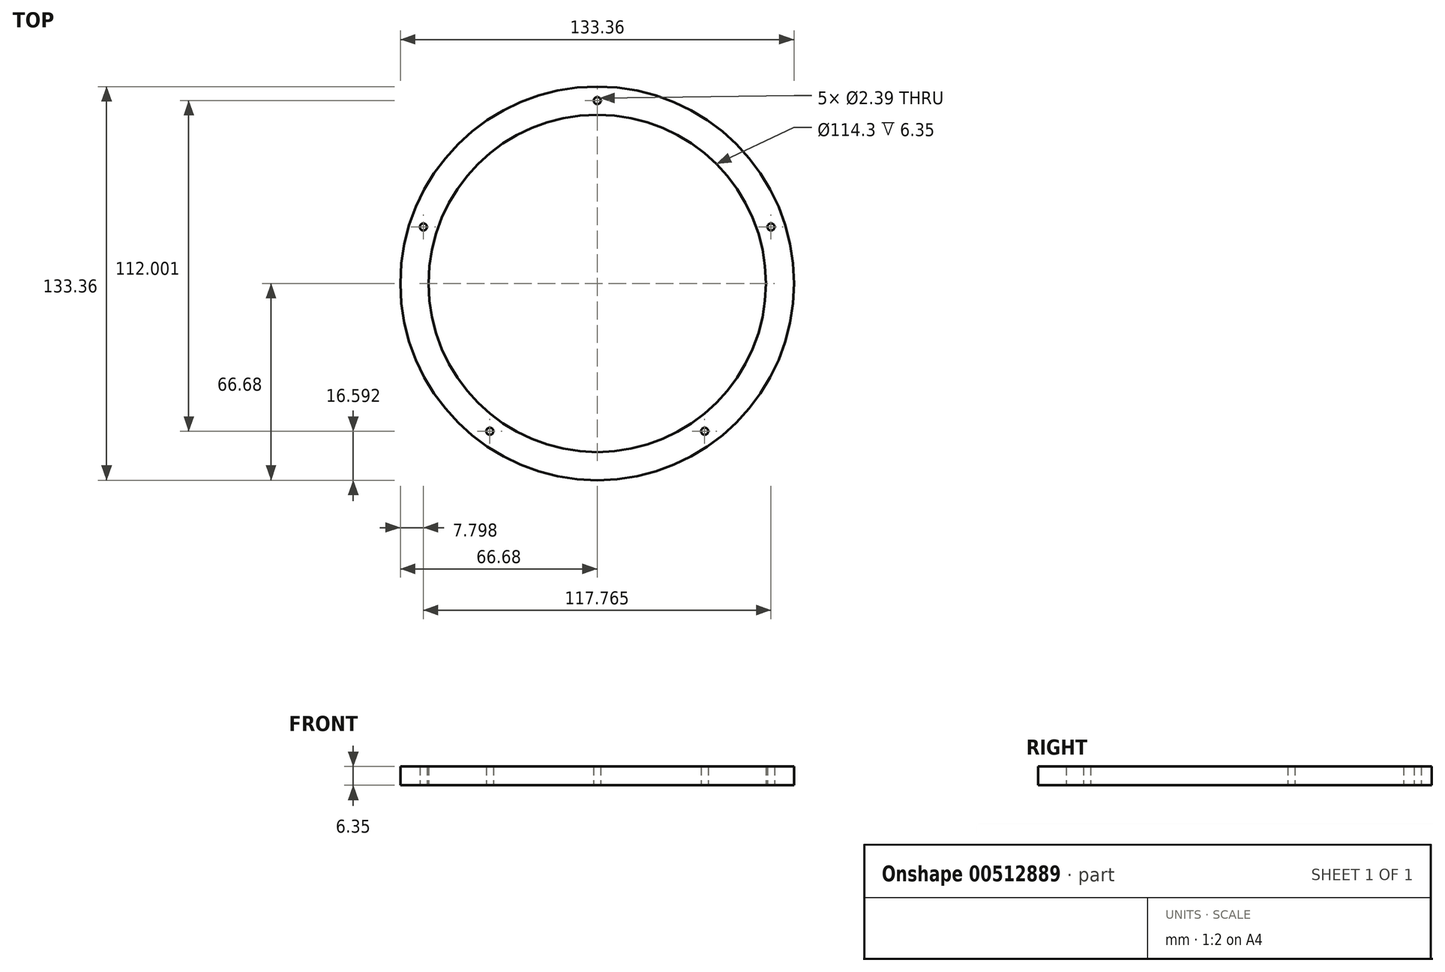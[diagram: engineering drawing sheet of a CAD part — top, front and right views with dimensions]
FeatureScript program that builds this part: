
annotation { "Feature Type Name" : "Feature", "Feature Type Description" : "" }
export const myFeature = defineFeature(function(context is Context, id is Id, definition is map)
    precondition{}
    {
        {
            var Q0;
            Q0=qCreatedBy(makeId("Top.planeOp"),FACE);
            var sketch = newSketch(context, id + "F0", { "sketchPlane" : qUnion([Q0])});
            skCircle(sketch, "E0", {"center": v(0, 0) * mm, "radius": 57.15 * mm});
            skCircle(sketch, "E1", {"center": v(0, 0) * mm, "radius": 66.68 * mm});
            skLineSegment(sketch, "E2", {"start": v(0, 57.15) * mm, "end": v(0, 66.68) * mm, "construction": true});
            skCircle(sketch, "E3", {"center": v(0, 61.91) * mm, "radius": 1.2 * mm});
            skCircle(sketch, "E4.1.0", {"center": v(-58.88, 19.13) * mm, "radius": 1.2 * mm});
            skCircle(sketch, "E4.2.0", {"center": v(-36.4, -50.09) * mm, "radius": 1.2 * mm});
            skCircle(sketch, "E4.3.0", {"center": v(36.4, -50.09) * mm, "radius": 1.2 * mm});
            skCircle(sketch, "E4.4.0", {"center": v(58.88, 19.13) * mm, "radius": 1.2 * mm});
            skSolve(sketch);
        }
        {
            var Q0;
            Q0 = qSketchRegion(id + "F0", true);
            extrude(context, id + "F1", {"entities" : qUnion([Q0]), "depth" : 6.35 * mm});
        }
    });
